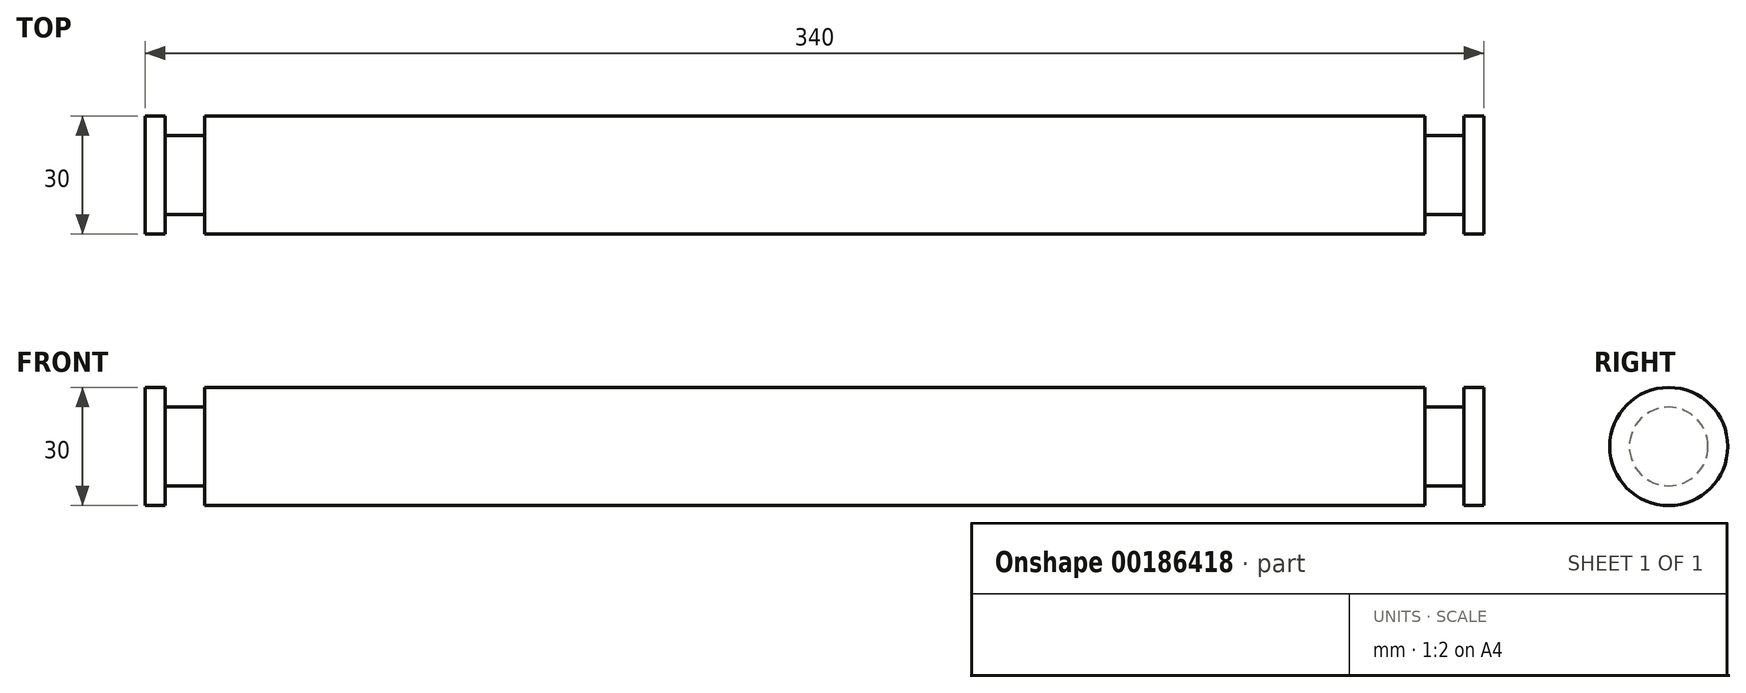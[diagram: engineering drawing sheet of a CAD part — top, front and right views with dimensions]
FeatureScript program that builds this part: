
annotation { "Feature Type Name" : "Feature", "Feature Type Description" : "" }
export const myFeature = defineFeature(function(context is Context, id is Id, definition is map)
    precondition{}
    {
        {
            var Q0;
            Q0=qCreatedBy(makeId("Front.planeOp"),FACE);
            var sketch = newSketch(context, id + "F0", { "sketchPlane" : qUnion([Q0])});
            skLineSegment(sketch, "E0", {"start": v(0, 0) * mm, "end": v(340, 0) * mm});
            skLineSegment(sketch, "E1", {"start": v(340, 0) * mm, "end": v(340, 15) * mm});
            skLineSegment(sketch, "E2", {"start": v(325, 10) * mm, "end": v(325, 15) * mm});
            skLineSegment(sketch, "E3", {"start": v(325, 15) * mm, "end": v(15, 15) * mm});
            skLineSegment(sketch, "E4", {"start": v(15, 15) * mm, "end": v(15, 10) * mm});
            skLineSegment(sketch, "E5", {"start": v(0, 15) * mm, "end": v(0, 0) * mm});
            skLineSegment(sketch, "E6", {"start": v(325, 10) * mm, "end": v(335, 10) * mm});
            skLineSegment(sketch, "E7", {"start": v(335, 10) * mm, "end": v(335, 15) * mm});
            skLineSegment(sketch, "E8", {"start": v(335, 15) * mm, "end": v(340, 15) * mm});
            skLineSegment(sketch, "E9", {"start": v(15, 10) * mm, "end": v(5, 10) * mm});
            skLineSegment(sketch, "E10", {"start": v(5, 10) * mm, "end": v(5, 15) * mm});
            skLineSegment(sketch, "E11", {"start": v(5, 15) * mm, "end": v(0, 15) * mm});
            skSolve(sketch);
        }
        {
            var Q0;
            Q0 = qSketchRegion(id + "F0", true);
            var Q1;
            Q1=sQuery(id+"F0.wireOp",EDGE,"E0");
            revolve(context, id + "F1", {"entities" : qUnion([Q0]), "axis" : qUnion([Q1]), "revolveType" : RevolveType.FULL});
        }
    });
